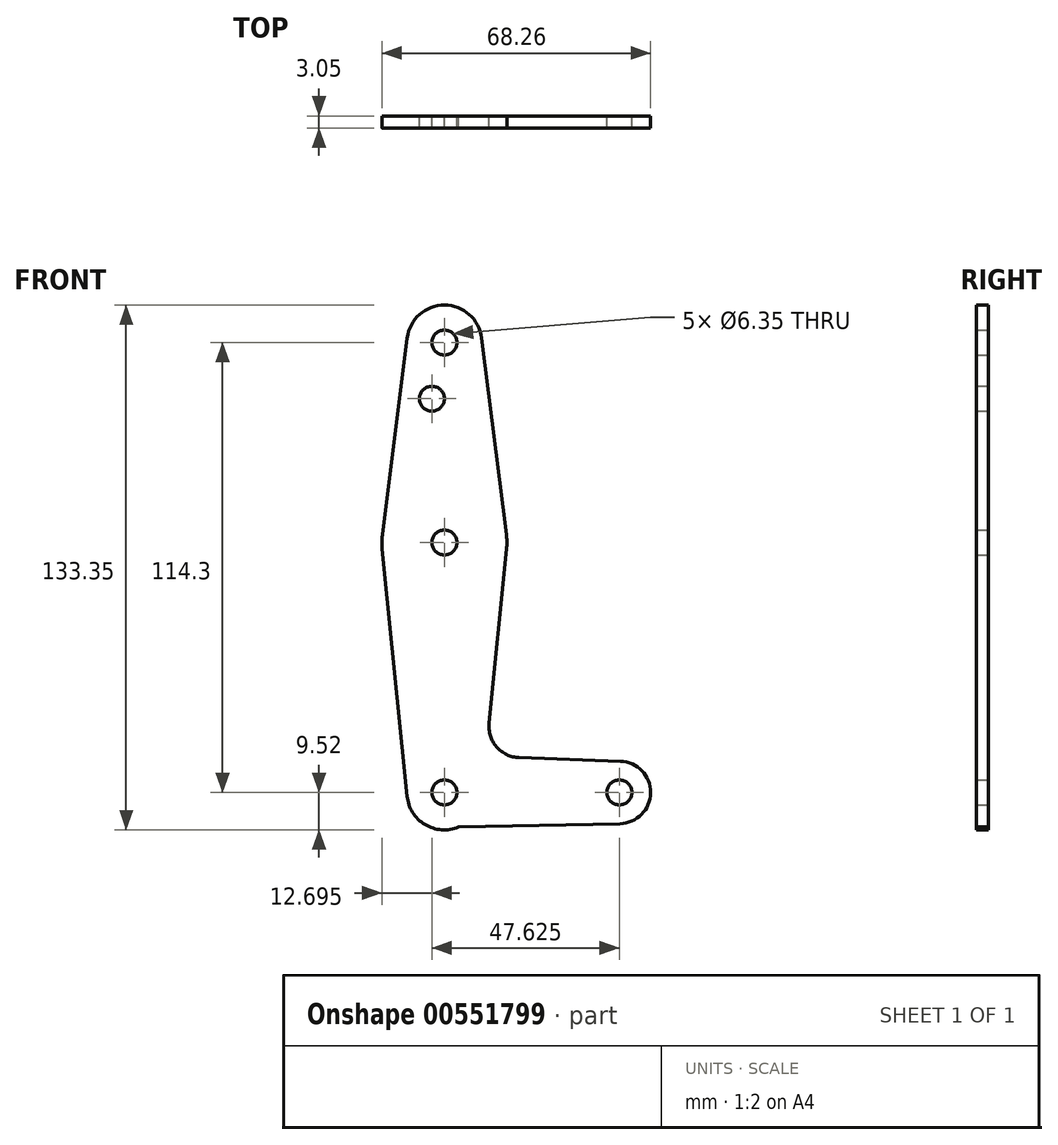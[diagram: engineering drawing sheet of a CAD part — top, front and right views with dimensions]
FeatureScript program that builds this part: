
annotation { "Feature Type Name" : "Feature", "Feature Type Description" : "" }
export const myFeature = defineFeature(function(context is Context, id is Id, definition is map)
    precondition{}
    {
        {
            var Q0;
            Q0=qCreatedBy(makeId("Front.planeOp"),FACE);
            var sketch = newSketch(context, id + "F0", { "sketchPlane" : qUnion([Q0])});
            skLineSegment(sketch, "E0", {"start": v(0, 0) * mm, "end": v(0, 114.3) * mm, "construction": true});
            skLineSegment(sketch, "E1", {"start": v(0, 0) * mm, "end": v(44.45, 0) * mm, "construction": true});
            skCircle(sketch, "E2", {"center": v(0, 114.3) * mm, "radius": 9.53 * mm});
            skCircle(sketch, "E3", {"center": v(0, 0) * mm, "radius": 9.53 * mm});
            skCircle(sketch, "E4", {"center": v(44.45, 0) * mm, "radius": 7.94 * mm});
            skCircle(sketch, "E5", {"center": v(0, 63.5) * mm, "radius": 15.88 * mm});
            skLineSegment(sketch, "E6", {"start": v(-9.45, 115.5) * mm, "end": v(-15.75, 65.48) * mm});
            skLineSegment(sketch, "E7", {"start": v(9.45, 115.5) * mm, "end": v(15.75, 65.48) * mm});
            skCircle(sketch, "E8", {"center": v(-3.18, 100.03) * mm, "radius": 3.18 * mm});
            skCircle(sketch, "E9", {"center": v(0, 114.3) * mm, "radius": 3.18 * mm});
            skCircle(sketch, "E10", {"center": v(0, 63.5) * mm, "radius": 3.18 * mm});
            skCircle(sketch, "E11", {"center": v(0, 0) * mm, "radius": 3.18 * mm});
            skCircle(sketch, "E12", {"center": v(44.45, 0) * mm, "radius": 3.18 * mm});
            skLineSegment(sketch, "E13", {"start": v(-15.8, 61.91) * mm, "end": v(-9.48, -0.95) * mm});
            skLineSegment(sketch, "E14", {"start": v(3.6, -8.82) * mm, "end": v(44.62, -7.94) * mm});
            skLineSegment(sketch, "E15", {"start": v(15.8, 61.91) * mm, "end": v(11.34, 17.6) * mm});
            skLineSegment(sketch, "E16", {"start": v(18.97, 8.85) * mm, "end": v(44.73, 7.93) * mm});
            skArc(sketch, "E17.filletArc", {"start": v(11.34, 17.6) * mm, "mid": v(13.26, 11.57) * mm, "end": v(18.97, 8.85) * mm});
            skSolve(sketch);
        }
        {
            var Q0;
            Q0 = qSketchRegion(id + "F0", true);
            var Q1;
            Q1=makeQuery(id+"F0.imprint","IMPRINT",FACE,{"disambiguationData":[TD([[makeQuery(id+"F0.imprint","IMPRINT",EDGE,{"derivedFrom":sQuery(id+"F0.wireOp",EDGE,"SXtUwe6s-ODsZ-9I4v-Kzm5-5L9fLP9RRPfq")}),1.0]])]});
            extrude(context, id + "F1", {"entities" : qUnion([Q0, Q1]), "depth" : 3.05 * mm, "offsetDistance" : 25.4 * mm});
        }
    });
